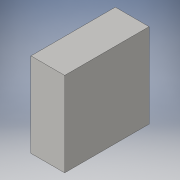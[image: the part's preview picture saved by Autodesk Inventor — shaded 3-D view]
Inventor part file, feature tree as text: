
AUTODESK INVENTOR PART (.ipt)
format: ipt  version: 2016 (Build 200138000, 138)  size: 82,432 bytes
history: native  units: in
note: dims shown in document units (in); Inventor stores cm internally (conversion verified against a paired STEP export)
features: extrude x1, sketch x1
ambient origin geometry x8: Origin, YZ Plane, XZ Plane, XY Plane, X Axis, Y Axis, Z Axis, Center Point
bodies: Solid1 (feature_tree)
feature tree (2):
  extrude  "Extrusion1"  Depth=1.9685in
  sketch  "Sketch1"  dims[d0=0.7874in d1=1.9685in d2=1.9685in d3=0.0in]
